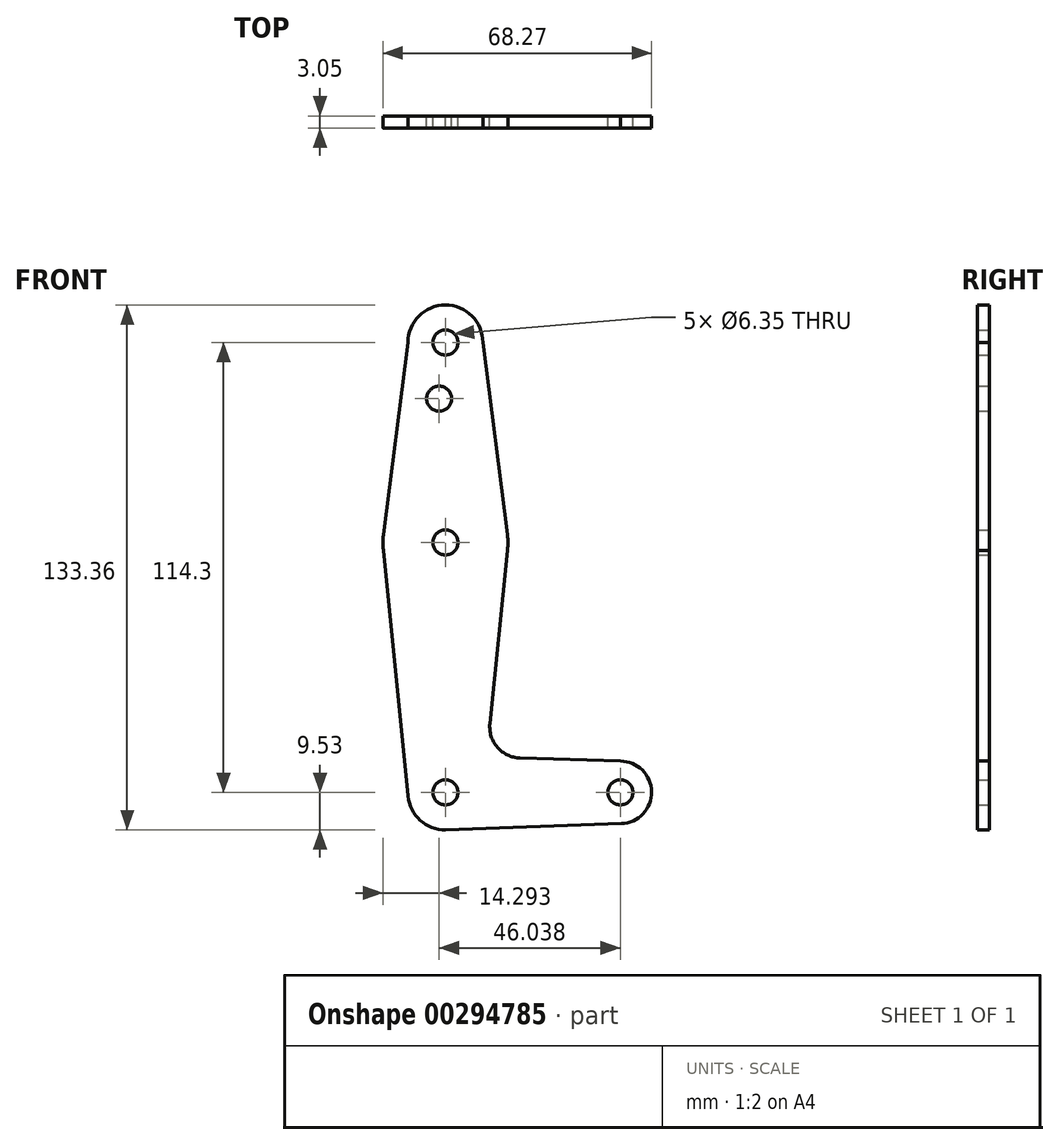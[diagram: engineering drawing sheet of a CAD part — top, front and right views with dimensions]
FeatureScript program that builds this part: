
annotation { "Feature Type Name" : "Feature", "Feature Type Description" : "" }
export const myFeature = defineFeature(function(context is Context, id is Id, definition is map)
    precondition{}
    {
        {
            var Q0;
            Q0=qCreatedBy(makeId("Front.planeOp"),FACE);
            var sketch = newSketch(context, id + "F0", { "sketchPlane" : qUnion([Q0])});
            skCircle(sketch, "E0", {"center": v(0, 0) * mm, "radius": 9.53 * mm});
            skCircle(sketch, "E1", {"center": v(44.45, 0) * mm, "radius": 7.94 * mm});
            skCircle(sketch, "E2", {"center": v(0, 63.5) * mm, "radius": 15.88 * mm});
            skCircle(sketch, "E3", {"center": v(0, 114.3) * mm, "radius": 9.53 * mm});
            skLineSegment(sketch, "E4", {"start": v(0, 114.3) * mm, "end": v(0, 63.5) * mm, "construction": true});
            skLineSegment(sketch, "E5", {"start": v(-9.53, 114.3) * mm, "end": v(-15.75, 65.5) * mm});
            skLineSegment(sketch, "E6", {"start": v(9.52, 114.3) * mm, "end": v(15.75, 65.5) * mm});
            skLineSegment(sketch, "E7", {"start": v(18.96, 8.74) * mm, "end": v(44.45, 7.94) * mm});
            skLineSegment(sketch, "E8", {"start": v(0, -9.52) * mm, "end": v(44.73, -7.93) * mm});
            skCircle(sketch, "E9", {"center": v(0, 114.3) * mm, "radius": 3.18 * mm});
            skCircle(sketch, "E10", {"center": v(0, 63.5) * mm, "radius": 3.18 * mm});
            skCircle(sketch, "E11", {"center": v(44.45, 0) * mm, "radius": 3.18 * mm});
            skLineSegment(sketch, "E12", {"start": v(15.75, 61.5) * mm, "end": v(11.3, 17.48) * mm});
            skLineSegment(sketch, "E13", {"start": v(-15.75, 61.5) * mm, "end": v(-9.48, -0.95) * mm});
            skCircle(sketch, "E14", {"center": v(0, 0) * mm, "radius": 3.18 * mm});
            skArc(sketch, "E15.filletArc", {"start": v(11.3, 17.48) * mm, "mid": v(13.22, 11.44) * mm, "end": v(18.96, 8.74) * mm});
            skLineSegment(sketch, "E16", {"start": v(0, 63.5) * mm, "end": v(0, 0) * mm, "construction": true});
            skLineSegment(sketch, "E17", {"start": v(0, 0) * mm, "end": v(44.45, 0) * mm, "construction": true});
            skCircle(sketch, "E18", {"center": v(-1.59, 100.03) * mm, "radius": 3.18 * mm});
            skSolve(sketch);
        }
        {
            var Q0;
            Q0=makeQuery(id+"F0.imprint","IMPRINT",FACE,{"disambiguationData":[TD([[makeQuery(id+"F0.imprint","IMPRINT",EDGE,{"derivedFrom":sQuery(id+"F0.wireOp",EDGE,"E9")}),-1.0]])]});
            var Q1;
            {var subQ1=sQuery(id+"F0.wireOp",EDGE,"E5");Q1=makeQuery(id+"F0.imprint","IMPRINT",FACE,{"disambiguationData":[TD([[makeQuery(id+"F0.imprint","IMPRINT",EDGE,{"derivedFrom":subQ1}),1.0]])]});}
            var Q2;
            Q2=makeQuery(id+"F0.imprint","IMPRINT",FACE,{"disambiguationData":[TD([[makeQuery(id+"F0.imprint","IMPRINT",EDGE,{"derivedFrom":sQuery(id+"F0.wireOp",EDGE,"E10")}),-1.0]])]});
            var Q3;
            {var subQ0=sQuery(id+"F0.wireOp",EDGE,"E7");Q3=makeQuery(id+"F0.imprint","IMPRINT",FACE,{"disambiguationData":[TD([[makeQuery(id+"F0.imprint","IMPRINT",EDGE,{"derivedFrom":subQ0}),-1.0]])]});}
            var Q4;
            Q4=makeQuery(id+"F0.imprint","IMPRINT",FACE,{"disambiguationData":[TD([[makeQuery(id+"F0.imprint","IMPRINT",EDGE,{"derivedFrom":sQuery(id+"F0.wireOp",EDGE,"E14")}),-1.0]])]});
            var Q5;
            Q5=makeQuery(id+"F0.imprint","IMPRINT",FACE,{"disambiguationData":[TD([[makeQuery(id+"F0.imprint","IMPRINT",EDGE,{"derivedFrom":sQuery(id+"F0.wireOp",EDGE,"E11")}),-1.0]])]});
            extrude(context, id + "F1", {"entities" : qUnion([Q0, Q1, Q2, Q3, Q4, Q5]), "depth" : 3.05 * mm});
        }
    });
